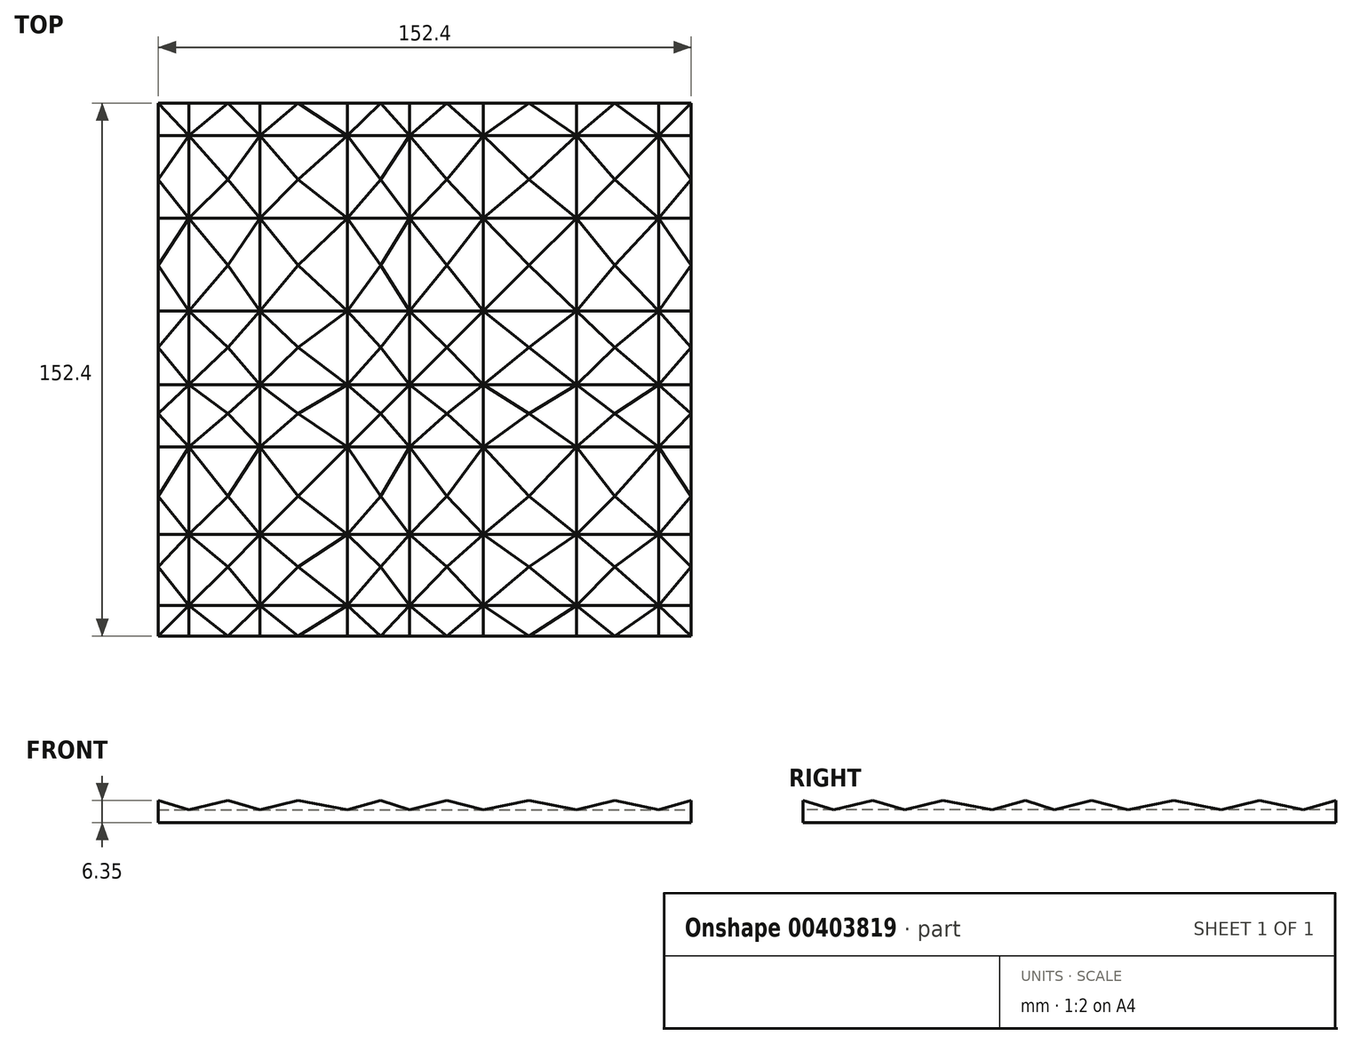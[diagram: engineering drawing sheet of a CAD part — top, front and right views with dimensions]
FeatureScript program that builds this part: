
annotation { "Feature Type Name" : "Feature", "Feature Type Description" : "" }
export const myFeature = defineFeature(function(context is Context, id is Id, definition is map)
    precondition{}
    {
        {
            var Q0;
            Q0=qCreatedBy(makeId("Front.planeOp"),FACE);
            var sketch = newSketch(context, id + "F0", { "sketchPlane" : qUnion([Q0])});
            skLineSegment(sketch, "E0", {"start": v(0, 0) * mm, "end": v(152.4, 0) * mm});
            skLineSegment(sketch, "E1", {"start": v(152.4, 0) * mm, "end": v(152.4, 6.35) * mm});
            skPoint(sketch, "E2.1.internal.snap0", {"position": v(152.4, 3.17) * mm});
            skPoint(sketch, "E2.3.internal.snap0", {"position": v(152.4, 3.17) * mm});
            skPoint(sketch, "E2.5.internal.snap0", {"position": v(152.4, 3.17) * mm});
            skFitSpline(sketch, "E2", {"points": [v(152.4, 6.35) * mm, v(131.62, 3.46) * mm, v(115.4, 5.48) * mm, v(100.41, 3.5) * mm, v(84.58, 6.65) * mm, v(71.64, 3.18) * mm, v(54.87, 6.91) * mm, v(40.94, 3.77) * mm, v(26.36, 6.52) * mm, v(13.13, 3.11) * mm, v(-1.3, 3.46) * mm], "startDerivative": vector(-351.44, 2.76) * mm, "endDerivative": vector(48.3, -193.7) * mm});
            skLineSegment(sketch, "E3", {"start": v(0, 6.3) * mm, "end": v(0, 0) * mm});
            skSolve(sketch);
        }
        {
            var Q0;
            Q0=qCreatedBy(makeId("Right.planeOp"),FACE);
            var sketch = newSketch(context, id + "F1", { "sketchPlane" : qUnion([Q0])});
            skLineSegment(sketch, "E4", {"start": v(0, 0) * mm, "end": v(152.4, 0) * mm});
            skLineSegment(sketch, "E5", {"start": v(152.4, 0) * mm, "end": v(152.4, 6.35) * mm});
            skFitSpline(sketch, "E6", {"points": [v(152.4, 6.35) * mm, v(135.41, 3.38) * mm, v(118.93, 5.86) * mm, v(105.06, 3.52) * mm, v(92.83, 6.82) * mm, v(78, 3.25) * mm, v(66.6, 7.1) * mm, v(56.43, 3.25) * mm, v(43.38, 6.4) * mm, v(24.42, 5.86) * mm, v(11.79, 3.38) * mm, v(0, 6.35) * mm], "startDerivative": vector(-140.77, -23.48) * mm, "endDerivative": vector(-154.64, 9.6) * mm});
            skLineSegment(sketch, "E7", {"start": v(0, 6.35) * mm, "end": v(0, 0) * mm});
            skSolve(sketch);
        }
        {
            var Q0;
            Q0=makeQuery(id+"F1.imprint","IMPRINT",FACE,{"disambiguationData":[TD([[makeQuery(id+"F1.imprint","IMPRINT",EDGE,{"derivedFrom":sQuery(id+"F1.wireOp",EDGE,"E4")}),1.0]])]});
            extrude(context, id + "F2", {"entities" : qUnion([Q0]), "depth" : 152.4 * mm});
        }
        {
            var Q0;
            Q0=makeQuery(id+"F0.imprint","IMPRINT",FACE,{"disambiguationData":[TD([[makeQuery(id+"F0.imprint","IMPRINT",EDGE,{"derivedFrom":sQuery(id+"F0.wireOp",EDGE,"E0")}),1.0]])]});
            extrude(context, id + "F3", {"entities" : qUnion([Q0]), "operationType" : NewBodyOperationType.INTERSECT, "depth" : -152.4 * mm});
        }
        {
            var Q0;
            Q0=qCreatedBy(makeId("Front.planeOp"),FACE);
            var sketch = newSketch(context, id + "F4", { "sketchPlane" : qUnion([Q0])});
            skLineSegment(sketch, "E8", {"start": v(0, 0) * mm, "end": v(-152.4, 0) * mm});
            skLineSegment(sketch, "E9", {"start": v(-152.4, 0) * mm, "end": v(-152.4, 6.35) * mm});
            skLineSegment(sketch, "E10", {"start": v(-152.4, 6.35) * mm, "end": v(-143.7, 3.64) * mm});
            skLineSegment(sketch, "E11", {"start": v(-9.35, 3.64) * mm, "end": v(0, 6.35) * mm});
            skLineSegment(sketch, "E12", {"start": v(0, 6.35) * mm, "end": v(0, 0) * mm});
            skLineSegment(sketch, "E13", {"start": v(-143.7, 3.64) * mm, "end": v(-132.55, 6.35) * mm});
            skLineSegment(sketch, "E14", {"start": v(-132.55, 6.35) * mm, "end": v(-123.32, 3.64) * mm});
            skLineSegment(sketch, "E15", {"start": v(-123.32, 3.64) * mm, "end": v(-112.4, 6.35) * mm});
            skLineSegment(sketch, "E16", {"start": v(-112.4, 6.35) * mm, "end": v(-98.29, 3.64) * mm});
            skLineSegment(sketch, "E17", {"start": v(-98.29, 3.64) * mm, "end": v(-88.78, 6.35) * mm});
            skLineSegment(sketch, "E18", {"start": v(-88.78, 6.35) * mm, "end": v(-80.57, 3.64) * mm});
            skLineSegment(sketch, "E19", {"start": v(-80.57, 3.64) * mm, "end": v(-69.87, 6.35) * mm});
            skLineSegment(sketch, "E20", {"start": v(-69.87, 6.35) * mm, "end": v(-59.5, 3.64) * mm});
            skLineSegment(sketch, "E21", {"start": v(-59.5, 3.64) * mm, "end": v(-46.38, 6.35) * mm});
            skLineSegment(sketch, "E22", {"start": v(-46.38, 6.35) * mm, "end": v(-32.86, 3.64) * mm});
            skLineSegment(sketch, "E23", {"start": v(-32.86, 3.64) * mm, "end": v(-21.88, 6.35) * mm});
            skLineSegment(sketch, "E24", {"start": v(-21.88, 6.35) * mm, "end": v(-9.35, 3.64) * mm});
            skSolve(sketch);
        }
        {
            var Q0;
            Q0=qCreatedBy(makeId("Right.planeOp"),FACE);
            var sketch = newSketch(context, id + "F5", { "sketchPlane" : qUnion([Q0])});
            skLineSegment(sketch, "E25", {"start": v(152.4, 0) * mm, "end": v(0, 0) * mm});
            skLineSegment(sketch, "E26", {"start": v(0, 0) * mm, "end": v(0, 6.35) * mm});
            skLineSegment(sketch, "E27", {"start": v(0, 6.35) * mm, "end": v(8.7, 3.64) * mm});
            skLineSegment(sketch, "E28", {"start": v(143.05, 3.64) * mm, "end": v(152.4, 6.35) * mm});
            skLineSegment(sketch, "E29", {"start": v(152.4, 6.35) * mm, "end": v(152.4, 0) * mm});
            skLineSegment(sketch, "E30", {"start": v(8.7, 3.64) * mm, "end": v(19.85, 6.35) * mm});
            skLineSegment(sketch, "E31", {"start": v(19.85, 6.35) * mm, "end": v(29.08, 3.64) * mm});
            skLineSegment(sketch, "E32", {"start": v(29.08, 3.64) * mm, "end": v(40, 6.35) * mm});
            skLineSegment(sketch, "E33", {"start": v(40, 6.35) * mm, "end": v(54.11, 3.64) * mm});
            skLineSegment(sketch, "E34", {"start": v(54.11, 3.64) * mm, "end": v(63.62, 6.35) * mm});
            skLineSegment(sketch, "E35", {"start": v(63.62, 6.35) * mm, "end": v(71.83, 3.64) * mm});
            skLineSegment(sketch, "E36", {"start": v(71.83, 3.64) * mm, "end": v(82.53, 6.35) * mm});
            skLineSegment(sketch, "E37", {"start": v(82.53, 6.35) * mm, "end": v(92.9, 3.64) * mm});
            skLineSegment(sketch, "E38", {"start": v(92.9, 3.64) * mm, "end": v(106.02, 6.35) * mm});
            skLineSegment(sketch, "E39", {"start": v(106.02, 6.35) * mm, "end": v(119.54, 3.64) * mm});
            skLineSegment(sketch, "E40", {"start": v(119.54, 3.64) * mm, "end": v(130.52, 6.35) * mm});
            skLineSegment(sketch, "E41", {"start": v(130.52, 6.35) * mm, "end": v(143.05, 3.64) * mm});
            skSolve(sketch);
        }
        {
            var Q0;
            Q0 = qSketchRegion(id + "F4", true);
            extrude(context, id + "F6", {"entities" : qUnion([Q0]), "depth" : -152.4 * mm});
        }
        {
            var Q0;
            Q0 = qSketchRegion(id + "F5", true);
            extrude(context, id + "F7", {"entities" : qUnion([Q0]), "operationType" : NewBodyOperationType.INTERSECT, "depth" : -152.4 * mm});
        }
    });
